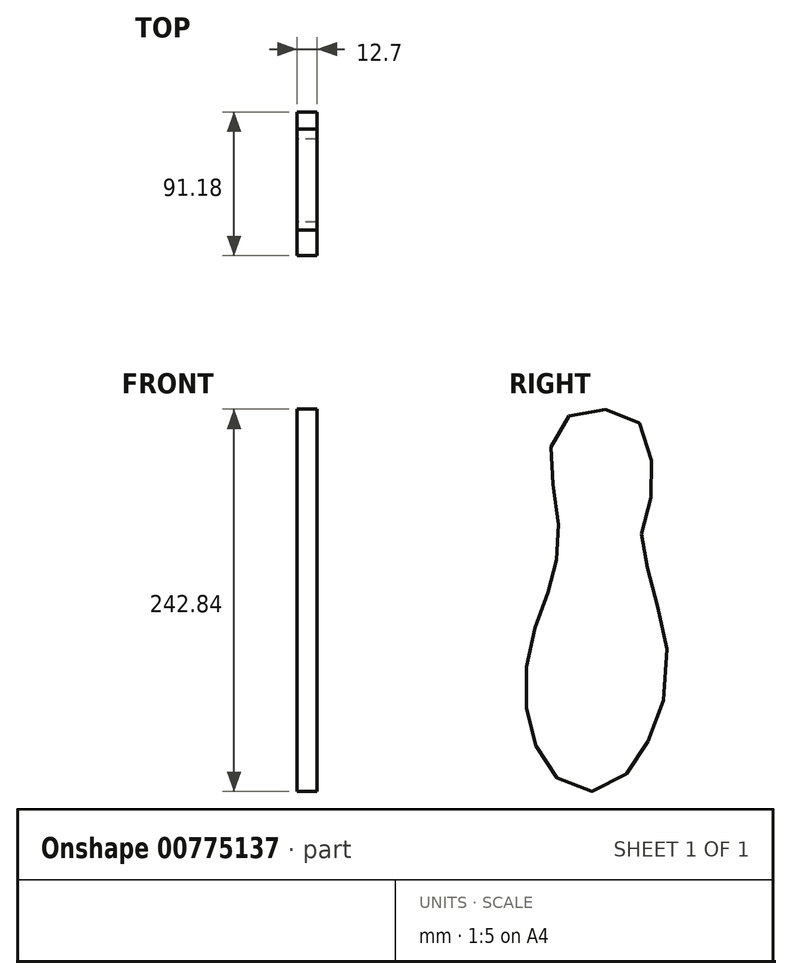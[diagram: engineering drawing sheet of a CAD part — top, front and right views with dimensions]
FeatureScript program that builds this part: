
annotation { "Feature Type Name" : "Feature", "Feature Type Description" : "" }
export const myFeature = defineFeature(function(context is Context, id is Id, definition is map)
    precondition{}
    {
        {
            var Q0;
            Q0=qCreatedBy(makeId("Right.planeOp"),FACE);
            var sketch = newSketch(context, id + "F0", { "sketchPlane" : qUnion([Q0])});
            skLineSegment(sketch, "E0.bottom", {"start": v(-76.2, 139.7) * mm, "end": v(76.2, 139.7) * mm});
            skLineSegment(sketch, "E0.top", {"start": v(-76.2, -139.7) * mm, "end": v(76.2, -139.7) * mm});
            skLineSegment(sketch, "E0.left", {"start": v(-76.2, 139.7) * mm, "end": v(-76.2, -139.7) * mm});
            skLineSegment(sketch, "E0.right", {"start": v(76.2, 139.7) * mm, "end": v(76.2, -139.7) * mm});
            skPoint(sketch, "E0.middle", {"position": v(0, 0) * mm});
            skFitSpline(sketch, "E1", {"points": [v(-32.16, 108.12) * mm, v(-40.3, 101.24) * mm, v(-43.42, 91.22) * mm, v(-44.05, 81.21) * mm, v(-43.42, 71.2) * mm, v(-40.92, 56.81) * mm, v(-39.05, 44.92) * mm, v(-39.05, 34.91) * mm, v(-39.05, 25.53) * mm, v(-40.3, 16.14) * mm, v(-42.8, 6.76) * mm, v(-44.68, 0) * mm, v(-47.18, -8.89) * mm, v(-50.93, -18.27) * mm, v(-54.69, -29.53) * mm, v(-56.56, -38.92) * mm, v(-59.7, -53.31) * mm, v(-60.32, -64.57) * mm, v(-59.07, -79.59) * mm, v(-56.56, -89.6) * mm, v(-53.44, -100.86) * mm, v(-49.06, -111.5) * mm, v(-42.17, -119.63) * mm, v(-32.16, -127.14) * mm, v(-22.78, -129.65) * mm, v(-10.26, -129.65) * mm, v(0, -122.76) * mm, v(7.26, -115.88) * mm, v(13.51, -107.12) * mm, v(19.14, -95.23) * mm, v(22.9, -85.22) * mm, v(29.78, -64.57) * mm, v(30.4, -43.93) * mm, v(28.53, -30.79) * mm, v(24.78, -16.4) * mm, v(21.02, 0) * mm, v(18.52, 8.63) * mm, v(16.02, 16.14) * mm, v(14.14, 25.53) * mm, v(14.14, 34.91) * mm, v(17.9, 46.17) * mm, v(19.77, 55.56) * mm, v(19.77, 66.2) * mm, v(19.77, 76.2) * mm, v(19.77, 87.47) * mm, v(15.4, 99.36) * mm, v(8.5, 107.5) * mm, v(0, 110) * mm, v(-12.77, 112.5) * mm, v(-22.78, 110.62) * mm, v(-32.16, 108.12) * mm]});
            skSolve(sketch);
        }
        {
            var Q0;
            Q0=makeQuery(id+"F0.imprint","IMPRINT",FACE,{"disambiguationData":[TD([[makeQuery(id+"F0.imprint","IMPRINT",EDGE,{"derivedFrom":sQuery(id+"F0.wireOp",EDGE,"E1")}),1.0]])]});
            extrude(context, id + "F1", {"entities" : qUnion([Q0]), "depth" : 12.7 * mm, "offsetDistance" : 25.4 * mm});
        }
    });
